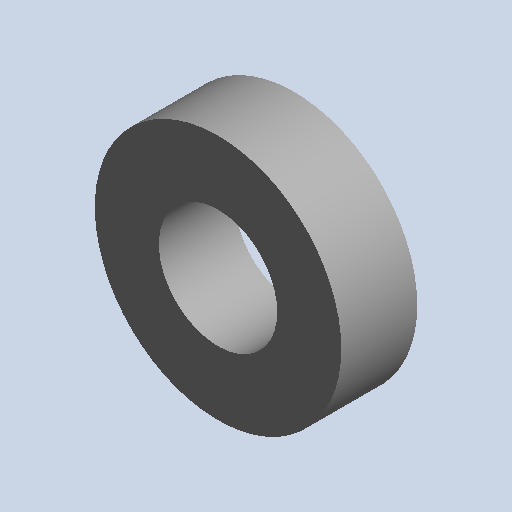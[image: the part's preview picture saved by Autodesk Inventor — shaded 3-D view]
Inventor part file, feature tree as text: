
AUTODESK INVENTOR PART (.ipt)
format: ipt  version: 2022.1 (Build 261234000, 234)  size: 68,096 bytes
history: native  units: mm (DEFAULTED — no unit token found)
features: other x8, extrude x1
bodies: Body1 (feature_tree)
feature tree (9):
  other  "Sólido1"
  other  "Origen"
  other  "Plano YZ"
  other  "Plano XZ"
  other  "Plano XY"
  other  "Eje X"
  other  "Eje Y"
  other  "Eje Z"
  extrude  "Extrude1"  [1 undecoded]
note: 1 required parameter value undecoded (feature->parameter linkage not recoverable at this tier; creation-order binding heuristic only, values carry confidence <= 0.55)
